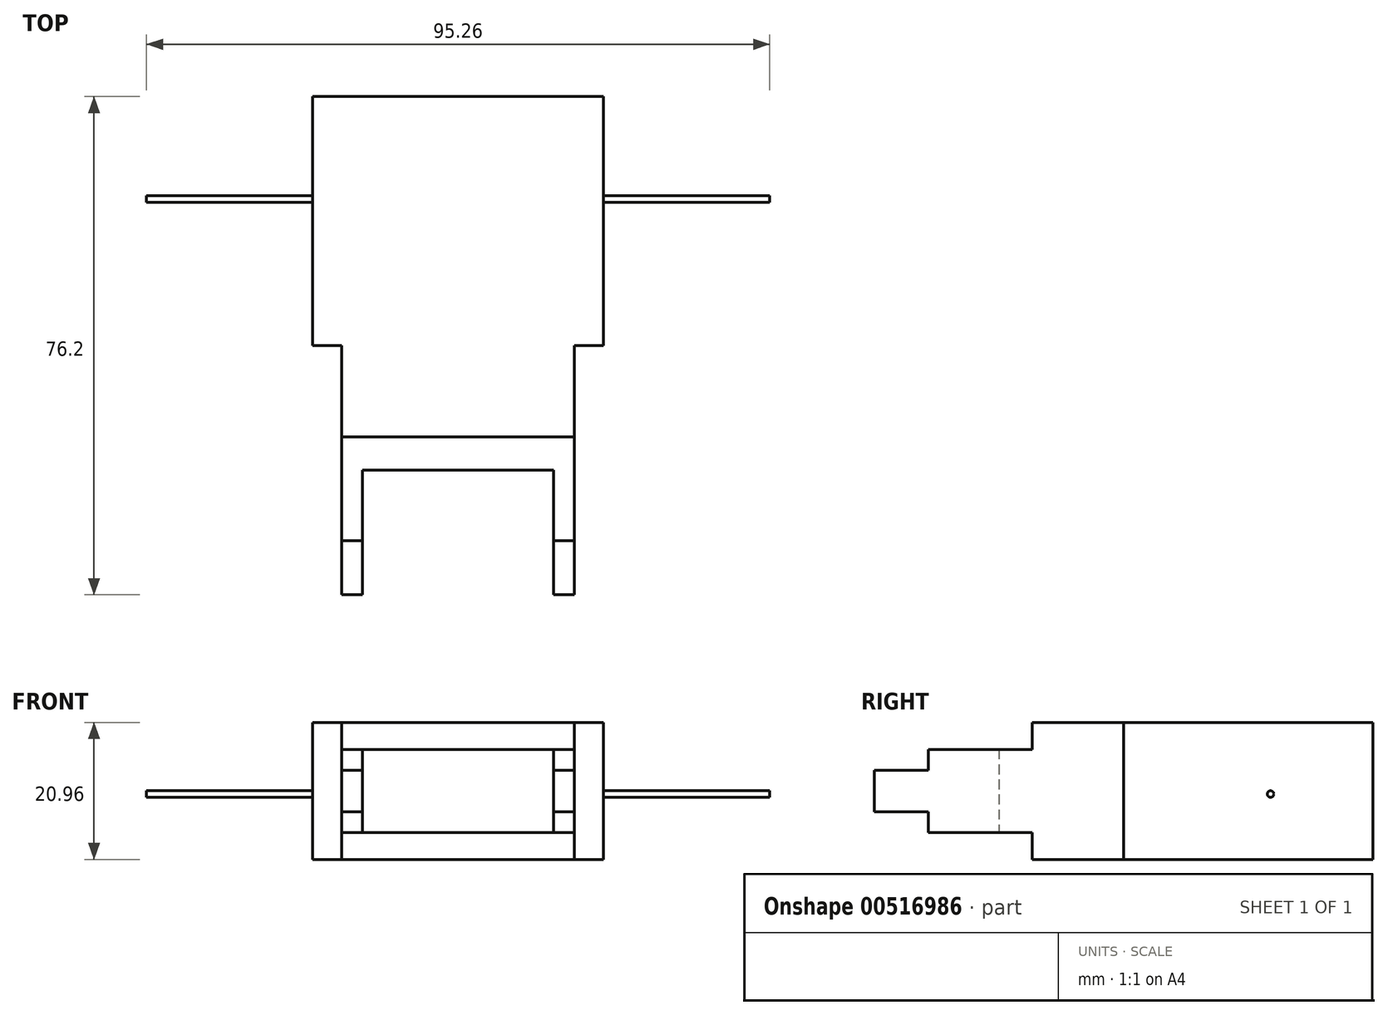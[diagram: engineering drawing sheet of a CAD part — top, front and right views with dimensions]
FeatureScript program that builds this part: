
annotation { "Feature Type Name" : "Feature", "Feature Type Description" : "" }
export const myFeature = defineFeature(function(context is Context, id is Id, definition is map)
    precondition{}
    {
        {
            var Q0;
            Q0=qCreatedBy(makeId("Top.planeOp"),FACE);
            var sketch = newSketch(context, id + "F0", { "sketchPlane" : qUnion([Q0])});
            skLineSegment(sketch, "E0.bottom", {"start": v(-22.22, 48.46) * mm, "end": v(22.23, 48.46) * mm});
            skLineSegment(sketch, "E0.top", {"start": v(-22.23, 10.36) * mm, "end": v(22.23, 10.36) * mm});
            skLineSegment(sketch, "E0.left", {"start": v(-22.22, 48.46) * mm, "end": v(-22.22, 10.36) * mm});
            skLineSegment(sketch, "E0.right", {"start": v(22.23, 48.46) * mm, "end": v(22.23, 10.36) * mm});
            skPoint(sketch, "E0.middle", {"position": v(0, 29.4) * mm});
            skLineSegment(sketch, "E1.bottom", {"start": v(-17.78, 10.36) * mm, "end": v(17.78, 10.36) * mm});
            skLineSegment(sketch, "E1.left", {"start": v(-17.78, 10.36) * mm, "end": v(-17.78, -27.74) * mm});
            skLineSegment(sketch, "E1.right", {"start": v(17.78, 10.36) * mm, "end": v(17.78, -27.74) * mm});
            skLineSegment(sketch, "E2", {"start": v(-17.78, -8.7) * mm, "end": v(17.78, -8.7) * mm});
            skLineSegment(sketch, "E3", {"start": v(-17.78, -27.74) * mm, "end": v(-14.6, -27.74) * mm});
            skLineSegment(sketch, "E4", {"start": v(-14.6, -27.74) * mm, "end": v(-14.6, -8.7) * mm});
            skLineSegment(sketch, "E5", {"start": v(17.78, -27.74) * mm, "end": v(14.6, -27.74) * mm});
            skLineSegment(sketch, "E6", {"start": v(14.6, -27.74) * mm, "end": v(14.6, -8.7) * mm});
            skSolve(sketch);
        }
        {
            var Q0;
            Q0 = qSketchRegion(id + "F0", true);
            extrude(context, id + "F1", {"entities" : qUnion([Q0]), "depth" : 20.95 * mm, "offsetDistance" : 25.4 * mm});
        }
        {
            var Q0;
            Q0=makeQuery(id+"F1.opExtrude","SWEPT_FACE",FACE,{"disambiguationData":[OSD([sQuery(id+"F0.wireOp",EDGE,"E1.left")])]});
            var sketch = newSketch(context, id + "F2", { "sketchPlane" : qUnion([Q0])});
            skLineSegment(sketch, "E7", {"start": v(27.74, 13.65) * mm, "end": v(19.49, 13.65) * mm});
            skLineSegment(sketch, "E8", {"start": v(19.49, 13.65) * mm, "end": v(19.49, 16.81) * mm});
            skLineSegment(sketch, "E9", {"start": v(19.49, 16.81) * mm, "end": v(3.61, 16.81) * mm});
            skLineSegment(sketch, "E10", {"start": v(3.61, 16.81) * mm, "end": v(3.61, 20.96) * mm});
            skLineSegment(sketch, "E11", {"start": v(3.61, 20.96) * mm, "end": v(27.74, 20.96) * mm});
            skLineSegment(sketch, "E12", {"start": v(27.74, 20.96) * mm, "end": v(27.74, 13.65) * mm});
            skLineSegment(sketch, "E13", {"start": v(27.74, 13.65) * mm, "end": v(27.74, 7.3) * mm});
            skLineSegment(sketch, "E14", {"start": v(27.74, 7.3) * mm, "end": v(19.49, 7.3) * mm});
            skLineSegment(sketch, "E15", {"start": v(19.49, 7.3) * mm, "end": v(19.49, 4.11) * mm});
            skLineSegment(sketch, "E16", {"start": v(19.49, 4.11) * mm, "end": v(3.61, 4.11) * mm});
            skLineSegment(sketch, "E17", {"start": v(3.61, 4.11) * mm, "end": v(3.61, 0) * mm});
            skLineSegment(sketch, "E18", {"start": v(3.61, 0) * mm, "end": v(27.74, 0) * mm});
            skLineSegment(sketch, "E19", {"start": v(27.74, 0) * mm, "end": v(27.74, 7.3) * mm});
            skSolve(sketch);
        }
        {
            var Q0;
            Q0=makeQuery(id+"F2.imprint","IMPRINT",FACE,{"disambiguationData":[TD([[makeQuery(id+"F2.imprint","IMPRINT",EDGE,{"derivedFrom":sQuery(id+"F2.wireOp",EDGE,"E7")}),-1.0]])]});
            var Q1;
            Q1=makeQuery(id+"F2.imprint","IMPRINT",FACE,{"disambiguationData":[TD([[makeQuery(id+"F2.imprint","IMPRINT",EDGE,{"derivedFrom":sQuery(id+"F2.wireOp",EDGE,"E14")}),1.0]])]});
            extrude(context, id + "F3", {"entities" : qUnion([Q0, Q1]), "operationType" : NewBodyOperationType.REMOVE, "oppositeDirection" : true, "depth" : 45.72 * mm, "offsetDistance" : 25.4 * mm});
        }
        {
            var Q0;
            Q0=makeQuery(id+"F1.opExtrude","SWEPT_FACE",FACE,{"disambiguationData":[OSD([sQuery(id+"F0.wireOp",EDGE,"E0.left")])]});
            var sketch = newSketch(context, id + "F4", { "sketchPlane" : qUnion([Q0])});
            skCircle(sketch, "E20", {"center": v(-32.8, 10) * mm, "radius": 0.5 * mm});
            skSolve(sketch);
        }
        {
            var Q0;
            Q0 = qSketchRegion(id + "F4", true);
            extrude(context, id + "F5", {"entities" : qUnion([Q0]), "operationType" : NewBodyOperationType.ADD, "depth" : 25.4 * mm, "offsetDistance" : 25.4 * mm});
        }
        {
            var Q0;
            Q0=makeQuery(id+"F1.opExtrude","SWEPT_BODY",BODY,{"disambiguationData":[OSD([sQuery(id+"F0.wireOp",EDGE,"E0.bottom"),sQuery(id+"F0.wireOp",EDGE,"E0.top"),sQuery(id+"F0.wireOp",EDGE,"E0.left"),sQuery(id+"F0.wireOp",EDGE,"E0.right"),sQuery(id+"F0.wireOp",EDGE,"E1.left"),sQuery(id+"F0.wireOp",EDGE,"E1.right"),sQuery(id+"F0.wireOp",EDGE,"E2"),sQuery(id+"F0.wireOp",EDGE,"E3"),sQuery(id+"F0.wireOp",EDGE,"E4"),sQuery(id+"F0.wireOp",EDGE,"E5"),sQuery(id+"F0.wireOp",EDGE,"E6")])]});
            var Q1;
            Q1=qCreatedBy(makeId("Right.planeOp"),FACE);
            mirror(context, id + "F6", {"operationType" : NewBodyOperationType.ADD, "entities" : qUnion([Q0]), "mirrorPlane" : qUnion([Q1])});
        }
    });
